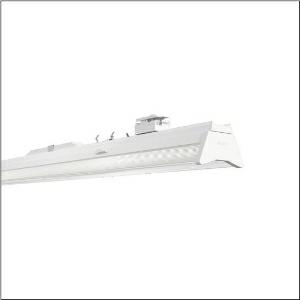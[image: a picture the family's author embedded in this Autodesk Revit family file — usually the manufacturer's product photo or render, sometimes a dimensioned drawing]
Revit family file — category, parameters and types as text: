
# Revit family: licross_r__11_performance_mo_51tm16dn4axg_9905
name_source: partatom
category: Lighting Fixtures
units: mm (PartAtom-declared; Revit-internal decimal feet)

## family parameters
Cut with Voids When Loaded = No
Host = Face
Light Source = No
Part Type = Normal
Room Calculation Point = No
Round Connector Dimension = Use Diameter
Shared = No

## types (1)
- --- (1 x LED, 10110 lm, 57.1 W, 4000K)
    Apparent Load = 57 VA
    CIE Flux Codes = 66 88 96 79 100
    Color Rendering = 80
    Color Temperature = 4000K
    Default Elevation = 1800 mm
    Description = Licross® 11 Performance MO, luminaire insert, of sheet steel, galvanised, coil coated, white, length: 1.500mm, width: 120mm, height: 123mm, LED rated luminous flux: 10.110lm, light colour: 840, control gear: DALI 2, with plug, 5-pole, with phase selection, mains connection: 220..240V, AC, 50/60Hz, rated input power: 57W, internal wiring halogen-free, primary light control with lens, of plastic, primary optical cover: cover, of PMMA, light emission: direct/indirect distribution, primary light characteristic: symmetric, protection rating (complete): IP40, insulation class (complete): insulation class I (protective earthing), certification: CE, ENEC, VDE, UKCA, protection symbol: D if used in an environment without relevant dust loads with corresponding accessories, impact resistance: IK06, permissible ambient temperature for indoor applications: -25..+35°C, corresponds to IFS (International Featured Standards) requirements for safety and quality in the food industry, reducing of maximum allowable ambient temperature of 5°C with ceiling mounting, LABS conformity tested according to VDMA 24364:2018-05, packaging unit: 1 piece
    Height = 114 mm
    Lamp = 1 x LED
    Lamp Light Flux = 10110 lm
    Lamp Power = 57.1 W
    Lamp count = 1
    Length = 1500 mm
    Luminous efficacy = 177 lm/W
    Manufacturer = Siteco
    ModVariant = No
    Model = 51TM16DN4AXG
    Mounting Place = Ceiling
    Mounting Type = Pendant
    Number of Poles = 1
    OnlyDefault = Yes
    Power Factor = 1
    Product Name = Licross® 11 Performance MO
    Product group = luminaire insert | ceiling pendant
    ProductGroupID = 902
    Protection Class = Protection class I
    Protection Degree = IP 40
    RLX_Detail_Level = 1
    RLX_Emergency_Light_Flux = 0 lm
    RLX_Emergency_Type = 0
    RLX_Emergency_Type_DB = No
    RlxData = <blob elided: 34061 chars, md5=0644b872>
    Socket = socket
    Standby Power = 0 W
    System Light Flux = 10110 lm
    System Power = 57 W
    Type Comments = factory setting: luminous flux: 100 % | dim-lin: 254 | 378 mA
    Type Image = l_1256138.jpg
    URL = http://relux.com
    VarID = @adj_122743
    Voltage = 0 V
    Weight = 0.00 kg
    Width = 120 mm

## geometry (parser evidence)
native form markers: Blend x4, Sweep x11
no freeform markers — native parametric forms only
